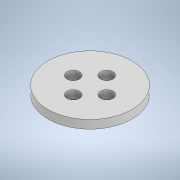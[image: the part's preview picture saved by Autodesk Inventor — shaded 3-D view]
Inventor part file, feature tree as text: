
AUTODESK INVENTOR PART (.ipt)
format: ipt  version: 2022 (Build 260153000, 153)  size: 109,056 bytes
history: native  units: mm
features: extrude x1, sketch x1
ambient origin geometry x8: Origin, YZ Plane, XZ Plane, XY Plane, X Axis, Y Axis, Z Axis, Center Point
bodies: Solid1 (feature_tree)
feature tree (2):
  extrude  "Extrusion1"  Depth=2.0mm
  sketch  "Sketch1"  dims[d0=20.0mm d2=3.0mm d3=40.0mm d5=360.0deg d7=2.0mm d8=0.0mm]
